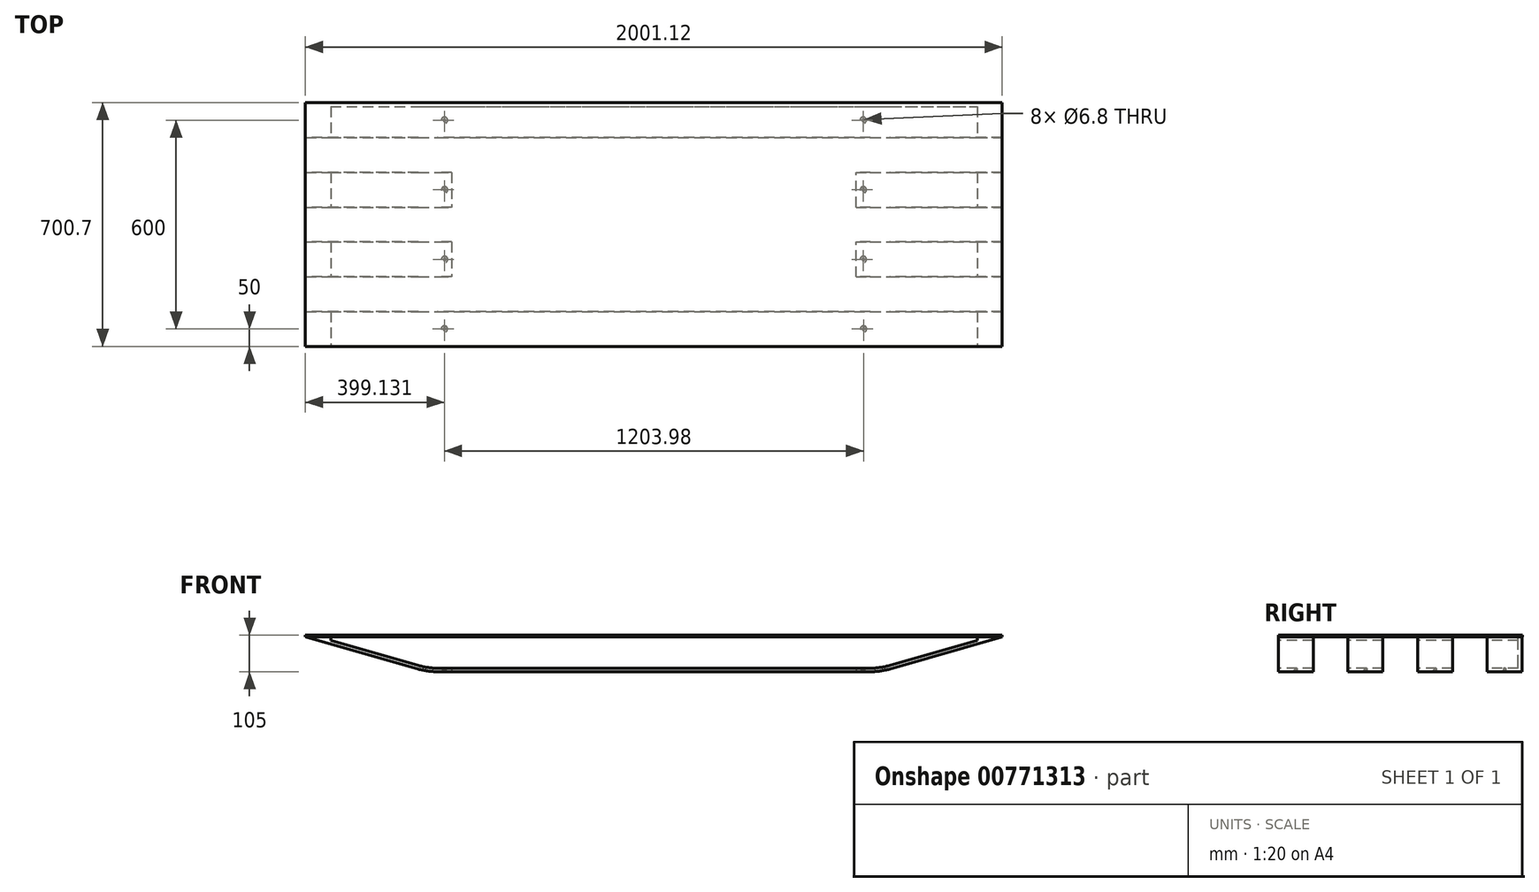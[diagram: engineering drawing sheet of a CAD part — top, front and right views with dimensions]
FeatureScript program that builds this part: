
annotation { "Feature Type Name" : "Feature", "Feature Type Description" : "" }
export const myFeature = defineFeature(function(context is Context, id is Id, definition is map)
    precondition{}
    {
        {
            var Q0;
            Q0=qCreatedBy(makeId("Front.planeOp"),FACE);
            var sketch = newSketch(context, id + "F0", { "sketchPlane" : qUnion([Q0])});
            skLineSegment(sketch, "E0.bottom", {"start": v(-1000, 50) * mm, "end": v(1000, 50) * mm});
            skLineSegment(sketch, "E0.top", {"start": v(-650, -50) * mm, "end": v(650, -50) * mm});
            skPoint(sketch, "E0.middle", {"position": v(0, 0) * mm});
            skLineSegment(sketch, "E1", {"start": v(-1000, 50) * mm, "end": v(-650, -50) * mm});
            skLineSegment(sketch, "E2", {"start": v(650, -50) * mm, "end": v(1000, 50) * mm});
            skPoint(sketch, "E0.left.end.orphan", {"position": v(-1000, -50) * mm});
            skPoint(sketch, "E0.right.end.orphan", {"position": v(1000, -50) * mm});
            skSolve(sketch);
        }
        {
            var Q0;
            Q0=makeQuery(id+"F0.imprint","IMPRINT",FACE,{"disambiguationData":[TD([[makeQuery(id+"F0.imprint","IMPRINT",EDGE,{"derivedFrom":sQuery(id+"F0.wireOp",EDGE,"E0.bottom")}),-1.0]])]});
            extrude(context, id + "F1", {"entities" : qUnion([Q0]), "oppositeDirection" : true, "depth" : 700 * mm, "offsetDistance" : 25 * mm});
        }
        {
            var Q0;
            Q0=makeQuery(id+"F1.opExtrude","SWEPT_FACE",FACE,{"disambiguationData":[OSD([sQuery(id+"F0.wireOp",EDGE,"E0.bottom")])]});
            var sketch = newSketch(context, id + "F2", { "sketchPlane" : qUnion([Q0])});
            skLineSegment(sketch, "E3", {"start": v(-1000, 600) * mm, "end": v(1000, 600) * mm});
            skLineSegment(sketch, "E4", {"start": v(-1000, 500) * mm, "end": v(1000, 500) * mm});
            skLineSegment(sketch, "E5", {"start": v(-1000, 400) * mm, "end": v(1000, 400) * mm});
            skLineSegment(sketch, "E6", {"start": v(-1000, 300) * mm, "end": v(1000, 300) * mm});
            skLineSegment(sketch, "E7", {"start": v(-1000, 200) * mm, "end": v(1000, 200) * mm});
            skLineSegment(sketch, "E8", {"start": v(-1000, 100) * mm, "end": v(1000, 100) * mm});
            skSolve(sketch);
        }
        {
            var Q0;
            {var subQ0=sQuery(id+"F2.wireOp",EDGE,"E3");Q0=makeQuery(id+"F2.imprint","IMPRINT",FACE,{"disambiguationData":[TD([[makeQuery(id+"F2.imprint","IMPRINT",EDGE,{"derivedFrom":subQ0}),-1.0]])]});}
            var Q1;
            {var subQ0=sQuery(id+"F2.wireOp",EDGE,"E5");Q1=makeQuery(id+"F2.imprint","IMPRINT",FACE,{"disambiguationData":[TD([[makeQuery(id+"F2.imprint","IMPRINT",EDGE,{"derivedFrom":subQ0}),-1.0]])]});}
            var Q2;
            {var subQ0=sQuery(id+"F2.wireOp",EDGE,"E7");Q2=makeQuery(id+"F2.imprint","IMPRINT",FACE,{"disambiguationData":[TD([[makeQuery(id+"F2.imprint","IMPRINT",EDGE,{"derivedFrom":subQ0}),-1.0]])]});}
            extrude(context, id + "F3", {"entities" : qUnion([Q0, Q1, Q2]), "operationType" : NewBodyOperationType.REMOVE, "oppositeDirection" : true, "depth" : 680 * mm, "offsetDistance" : 25 * mm});
        }
        {
            var Q0;
            Q0=makeQuery(id+"F1.opExtrude","CAP_FACE",FACE,{"disambiguationData":[OSD([sQuery(id+"F0.wireOp",EDGE,"E0.bottom"),sQuery(id+"F0.wireOp",EDGE,"E0.top"),sQuery(id+"F0.wireOp",EDGE,"E1"),sQuery(id+"F0.wireOp",EDGE,"E2")])],"isStart":true});
            var sketch = newSketch(context, id + "F4", { "sketchPlane" : qUnion([Q0])});
            skLineSegment(sketch, "E9.0", {"start": v(-928.6, 40) * mm, "end": v(928.6, 40) * mm});
            skLineSegment(sketch, "E9.1", {"start": v(-928.6, 40) * mm, "end": v(-648.6, -40) * mm});
            skLineSegment(sketch, "E9.2", {"start": v(-648.6, -40) * mm, "end": v(648.6, -40) * mm});
            skLineSegment(sketch, "E9.3", {"start": v(648.6, -40) * mm, "end": v(928.6, 40) * mm});
            skLineSegment(sketch, "E10", {"start": v(-928.6, 40) * mm, "end": v(-928.6, 50) * mm});
            skLineSegment(sketch, "E11", {"start": v(928.6, 40) * mm, "end": v(928.6, 50) * mm});
            skSolve(sketch);
        }
        {
            var Q0;
            Q0=makeQuery(id+"F4.imprint","IMPRINT",FACE,{"disambiguationData":[TD([[makeQuery(id+"F4.imprint","IMPRINT",EDGE,{"derivedFrom":sQuery(id+"F4.wireOp",EDGE,"E9.0")}),-1.0]])]});
            var Q1;
            Q1=makeQuery(id+"F4.imprint","IMPRINT",FACE,{"disambiguationData":[TD([[makeQuery(id+"F4.imprint","IMPRINT",EDGE,{"derivedFrom":sQuery(id+"F4.wireOp",EDGE,"E9.0")}),1.0]])]});
            extrude(context, id + "F5", {"entities" : qUnion([Q0, Q1]), "operationType" : NewBodyOperationType.REMOVE, "oppositeDirection" : true, "depth" : 689 * mm, "offsetDistance" : 25 * mm});
        }
        {
            var Q0;
            {var subQ2=sQuery(id+"F0.wireOp",EDGE,"E0.bottom");Q0=makeQuery(id+"F3.boolean.opBoolean","SPLIT",FACE,{"disambiguationData":[TD([makeQuery(id+"F3.opExtrude","SWEPT_FACE",FACE,{"disambiguationData":[OSD([sQuery(id+"F2.wireOp",EDGE,"E3")])]})])],"derivedFrom":makeQuery(id+"F1.opExtrude","SWEPT_FACE",FACE,{"disambiguationData":[OSD([subQ2])]})});}
            var sketch = newSketch(context, id + "F6", { "sketchPlane" : qUnion([Q0])});
            skLineSegment(sketch, "E12.bottom", {"start": v(-1000, 700) * mm, "end": v(1000.38, 700) * mm});
            skLineSegment(sketch, "E12.top", {"start": v(-1000, 0) * mm, "end": v(1000.38, 0) * mm});
            skLineSegment(sketch, "E12.left", {"start": v(-1000, 700) * mm, "end": v(-1000, 0) * mm});
            skLineSegment(sketch, "E12.right", {"start": v(1000.38, 700) * mm, "end": v(1000.38, 0) * mm});
            skLineSegment(sketch, "E13.0", {"start": v(-930, 680) * mm, "end": v(-930, 20) * mm});
            skLineSegment(sketch, "E13.1", {"start": v(-930, 680) * mm, "end": v(930.38, 680) * mm});
            skLineSegment(sketch, "E13.2", {"start": v(930.38, 680) * mm, "end": v(930.38, 20) * mm});
            skLineSegment(sketch, "E13.3", {"start": v(-930, 20) * mm, "end": v(930.38, 20) * mm});
            skSolve(sketch);
        }
        {
            var Q0;
            {var subQ0=sQuery(id+"F0.wireOp",EDGE,"E0.bottom");var subQ29=makeQuery(id+"F5.boolean.opBoolean","COPY",EDGE,{"derivedFrom":makeQuery(id+"F5.opExtrude","CAP_EDGE",EDGE,{"disambiguationData":[OSD([subQ0])],"isStart":false})});Q0=makeQuery(id+"F6.imprint","IMPRINT",FACE,{"disambiguationData":[TD([[makeQuery(id+"F6.imprint","IMPRINT",EDGE,{"derivedFrom":subQ29}),1.0]])]});}
            var Q1;
            {var subQ13=sQuery(id+"F6.wireOp",EDGE,"E12.top");Q1=makeQuery(id+"F6.imprint","IMPRINT",FACE,{"disambiguationData":[TD([[makeQuery(id+"F6.imprint","IMPRINT",EDGE,{"derivedFrom":subQ13}),1.0]])]});}
            extrude(context, id + "F7", {"entities" : qUnion([Q0, Q1]), "depth" : 10 * mm, "offsetDistance" : 25 * mm});
        }
        {
            var Q0;
            {var subQ0=sQuery(id+"F0.wireOp",EDGE,"E0.top");var subQ1=sQuery(id+"F0.wireOp",EDGE,"E1");Q0=makeQuery(id+"F3.boolean.opBoolean","SPLIT",EDGE,{"disambiguationData":[TD([makeQuery(id+"F3.opExtrude","SWEPT_FACE",FACE,{"disambiguationData":[OSD([sQuery(id+"F2.wireOp",EDGE,"E6")])]})])],"derivedFrom":makeQuery(id+"F1.opExtrude","SWEPT_EDGE",EDGE,{"disambiguationData":[OSD([subQ0,subQ1])]})});}
            var Q1;
            {var subQ0=sQuery(id+"F0.wireOp",EDGE,"E1");var subQ1=sQuery(id+"F0.wireOp",EDGE,"E0.top");Q1=makeQuery(id+"F3.boolean.opBoolean","SPLIT",EDGE,{"disambiguationData":[TD([makeQuery(id+"F3.opExtrude","SWEPT_FACE",FACE,{"disambiguationData":[OSD([sQuery(id+"F2.wireOp",EDGE,"E8")])]})])],"derivedFrom":makeQuery(id+"F1.opExtrude","SWEPT_EDGE",EDGE,{"disambiguationData":[OSD([subQ1,subQ0])]})});}
            var Q2;
            {var subQ0=sQuery(id+"F0.wireOp",EDGE,"E0.top");var subQ1=sQuery(id+"F0.wireOp",EDGE,"E1");Q2=makeQuery(id+"F3.boolean.opBoolean","SPLIT",EDGE,{"disambiguationData":[TD([makeQuery(id+"F3.opExtrude","SWEPT_FACE",FACE,{"disambiguationData":[OSD([sQuery(id+"F2.wireOp",EDGE,"E4")])]})])],"derivedFrom":makeQuery(id+"F1.opExtrude","SWEPT_EDGE",EDGE,{"disambiguationData":[OSD([subQ0,subQ1])]})});}
            var Q3;
            {var subQ0=sQuery(id+"F0.wireOp",EDGE,"E1");var subQ1=sQuery(id+"F0.wireOp",EDGE,"E0.top");Q3=makeQuery(id+"F3.boolean.opBoolean","SPLIT",EDGE,{"disambiguationData":[TD([makeQuery(id+"F3.opExtrude","SWEPT_FACE",FACE,{"disambiguationData":[OSD([sQuery(id+"F2.wireOp",EDGE,"E3")])]})])],"derivedFrom":makeQuery(id+"F1.opExtrude","SWEPT_EDGE",EDGE,{"disambiguationData":[OSD([subQ1,subQ0])]})});}
            var Q4;
            {var subQ0=sQuery(id+"F0.wireOp",EDGE,"E2");var subQ1=sQuery(id+"F0.wireOp",EDGE,"E0.top");Q4=makeQuery(id+"F3.boolean.opBoolean","SPLIT",EDGE,{"disambiguationData":[TD([makeQuery(id+"F3.opExtrude","SWEPT_FACE",FACE,{"disambiguationData":[OSD([sQuery(id+"F2.wireOp",EDGE,"E3")])]})])],"derivedFrom":makeQuery(id+"F1.opExtrude","SWEPT_EDGE",EDGE,{"disambiguationData":[OSD([subQ1,subQ0])]})});}
            var Q5;
            {var subQ0=sQuery(id+"F0.wireOp",EDGE,"E0.top");var subQ1=sQuery(id+"F0.wireOp",EDGE,"E2");Q5=makeQuery(id+"F3.boolean.opBoolean","SPLIT",EDGE,{"disambiguationData":[TD([makeQuery(id+"F3.opExtrude","SWEPT_FACE",FACE,{"disambiguationData":[OSD([sQuery(id+"F2.wireOp",EDGE,"E4")])]})])],"derivedFrom":makeQuery(id+"F1.opExtrude","SWEPT_EDGE",EDGE,{"disambiguationData":[OSD([subQ0,subQ1])]})});}
            var Q6;
            {var subQ0=sQuery(id+"F0.wireOp",EDGE,"E0.top");var subQ1=sQuery(id+"F0.wireOp",EDGE,"E2");Q6=makeQuery(id+"F3.boolean.opBoolean","SPLIT",EDGE,{"disambiguationData":[TD([makeQuery(id+"F3.opExtrude","SWEPT_FACE",FACE,{"disambiguationData":[OSD([sQuery(id+"F2.wireOp",EDGE,"E6")])]})])],"derivedFrom":makeQuery(id+"F1.opExtrude","SWEPT_EDGE",EDGE,{"disambiguationData":[OSD([subQ0,subQ1])]})});}
            var Q7;
            {var subQ0=sQuery(id+"F0.wireOp",EDGE,"E2");var subQ1=sQuery(id+"F0.wireOp",EDGE,"E0.top");Q7=makeQuery(id+"F3.boolean.opBoolean","SPLIT",EDGE,{"disambiguationData":[TD([makeQuery(id+"F3.opExtrude","SWEPT_FACE",FACE,{"disambiguationData":[OSD([sQuery(id+"F2.wireOp",EDGE,"E8")])]})])],"derivedFrom":makeQuery(id+"F1.opExtrude","SWEPT_EDGE",EDGE,{"disambiguationData":[OSD([subQ1,subQ0])]})});}
            var Q8;
            {var subQ0=sQuery(id+"F4.wireOp",EDGE,"E9.1");var subQ1=sQuery(id+"F4.wireOp",EDGE,"E9.2");Q8=makeQuery(id+"F5.boolean.opBoolean","COPY",EDGE,{"disambiguationData":[TD([makeQuery(id+"F3.boolean.opBoolean","COPY",FACE,{"derivedFrom":makeQuery(id+"F3.opExtrude","SWEPT_FACE",FACE,{"disambiguationData":[OSD([sQuery(id+"F2.wireOp",EDGE,"E6")])]})})])],"derivedFrom":makeQuery(id+"F5.opExtrude","SWEPT_EDGE",EDGE,{"disambiguationData":[OSD([subQ0,subQ1])]})});}
            var Q9;
            {var subQ0=sQuery(id+"F4.wireOp",EDGE,"E9.1");var subQ1=sQuery(id+"F4.wireOp",EDGE,"E9.2");Q9=makeQuery(id+"F5.boolean.opBoolean","COPY",EDGE,{"disambiguationData":[TD([makeQuery(id+"F3.boolean.opBoolean","COPY",FACE,{"derivedFrom":makeQuery(id+"F3.opExtrude","SWEPT_FACE",FACE,{"disambiguationData":[OSD([sQuery(id+"F2.wireOp",EDGE,"E8")])]})})])],"derivedFrom":makeQuery(id+"F5.opExtrude","SWEPT_EDGE",EDGE,{"disambiguationData":[OSD([subQ0,subQ1])]})});}
            var Q10;
            {var subQ0=sQuery(id+"F4.wireOp",EDGE,"E9.2");var subQ1=sQuery(id+"F4.wireOp",EDGE,"E9.1");Q10=makeQuery(id+"F5.boolean.opBoolean","COPY",EDGE,{"disambiguationData":[TD([makeQuery(id+"F3.boolean.opBoolean","COPY",FACE,{"derivedFrom":makeQuery(id+"F3.opExtrude","SWEPT_FACE",FACE,{"disambiguationData":[OSD([sQuery(id+"F2.wireOp",EDGE,"E4")])]})})])],"derivedFrom":makeQuery(id+"F5.opExtrude","SWEPT_EDGE",EDGE,{"disambiguationData":[OSD([subQ1,subQ0])]})});}
            var Q11;
            {var subQ0=sQuery(id+"F4.wireOp",EDGE,"E9.2");var subQ1=sQuery(id+"F4.wireOp",EDGE,"E9.1");Q11=makeQuery(id+"F5.boolean.opBoolean","COPY",EDGE,{"disambiguationData":[TD([makeQuery(id+"F3.boolean.opBoolean","COPY",FACE,{"derivedFrom":makeQuery(id+"F3.opExtrude","SWEPT_FACE",FACE,{"disambiguationData":[OSD([sQuery(id+"F2.wireOp",EDGE,"E3")])]})})])],"derivedFrom":makeQuery(id+"F5.opExtrude","SWEPT_EDGE",EDGE,{"disambiguationData":[OSD([subQ1,subQ0])]})});}
            var Q12;
            {var subQ0=sQuery(id+"F4.wireOp",EDGE,"E9.2");var subQ1=sQuery(id+"F4.wireOp",EDGE,"E9.3");Q12=makeQuery(id+"F5.boolean.opBoolean","COPY",EDGE,{"disambiguationData":[TD([makeQuery(id+"F3.boolean.opBoolean","COPY",FACE,{"derivedFrom":makeQuery(id+"F3.opExtrude","SWEPT_FACE",FACE,{"disambiguationData":[OSD([sQuery(id+"F2.wireOp",EDGE,"E6")])]})})])],"derivedFrom":makeQuery(id+"F5.opExtrude","SWEPT_EDGE",EDGE,{"disambiguationData":[OSD([subQ0,subQ1])]})});}
            var Q13;
            {var subQ0=sQuery(id+"F4.wireOp",EDGE,"E9.3");var subQ1=sQuery(id+"F4.wireOp",EDGE,"E9.2");Q13=makeQuery(id+"F5.boolean.opBoolean","COPY",EDGE,{"disambiguationData":[TD([makeQuery(id+"F3.boolean.opBoolean","COPY",FACE,{"derivedFrom":makeQuery(id+"F3.opExtrude","SWEPT_FACE",FACE,{"disambiguationData":[OSD([sQuery(id+"F2.wireOp",EDGE,"E8")])]})})])],"derivedFrom":makeQuery(id+"F5.opExtrude","SWEPT_EDGE",EDGE,{"disambiguationData":[OSD([subQ1,subQ0])]})});}
            var Q14;
            {var subQ0=sQuery(id+"F4.wireOp",EDGE,"E9.3");var subQ1=sQuery(id+"F4.wireOp",EDGE,"E9.2");Q14=makeQuery(id+"F5.boolean.opBoolean","COPY",EDGE,{"disambiguationData":[TD([makeQuery(id+"F3.boolean.opBoolean","COPY",FACE,{"derivedFrom":makeQuery(id+"F3.opExtrude","SWEPT_FACE",FACE,{"disambiguationData":[OSD([sQuery(id+"F2.wireOp",EDGE,"E3")])]})})])],"derivedFrom":makeQuery(id+"F5.opExtrude","SWEPT_EDGE",EDGE,{"disambiguationData":[OSD([subQ1,subQ0])]})});}
            fillet(context, id + "F8", {"entities" : qUnion([Q0, Q1, Q2, Q3, Q4, Q5, Q6, Q7, Q8, Q9, Q10, Q11, Q12, Q13, Q14]), "radius" : 200 * mm, "tangentPropagation" : true, "allowEdgeOverflow" : false});
        }
        {
            var Q0;
            {var subQ0=sQuery(id+"F4.wireOp",EDGE,"E9.2");var subQ1=sQuery(id+"F4.wireOp",EDGE,"E9.3");Q0=makeQuery(id+"F5.boolean.opBoolean","COPY",EDGE,{"disambiguationData":[TD([makeQuery(id+"F3.boolean.opBoolean","COPY",FACE,{"derivedFrom":makeQuery(id+"F3.opExtrude","SWEPT_FACE",FACE,{"disambiguationData":[OSD([sQuery(id+"F2.wireOp",EDGE,"E4")])]})})])],"derivedFrom":makeQuery(id+"F5.opExtrude","SWEPT_EDGE",EDGE,{"disambiguationData":[OSD([subQ0,subQ1])]})});}
            fillet(context, id + "F9", {"entities" : qUnion([Q0]), "radius" : 200 * mm, "tangentPropagation" : true, "allowEdgeOverflow" : false});
        }
        {
            var Q0;
            Q0=makeQuery(id+"F7.opExtrude","SWEPT_BODY",BODY,{"disambiguationData":[OSD([sQuery(id+"F0.wireOp",EDGE,"E0.bottom"),sQuery(id+"F4.wireOp",EDGE,"E10"),sQuery(id+"F4.wireOp",EDGE,"E11"),sQuery(id+"F6.wireOp",EDGE,"E12.bottom"),sQuery(id+"F6.wireOp",EDGE,"E12.top"),sQuery(id+"F6.wireOp",EDGE,"E12.left"),sQuery(id+"F6.wireOp",EDGE,"E12.right"),sQuery(id+"F6.wireOp",EDGE,"E13.0"),sQuery(id+"F6.wireOp",EDGE,"E13.1"),sQuery(id+"F6.wireOp",EDGE,"E13.2"),sQuery(id+"F6.wireOp",EDGE,"E13.3")])]});
            deleteBodies(context, id + "F10", {"entities" : qUnion([Q0])});
        }
        {
            var Q0;
            Q0=makeQuery(id+"F5.boolean.opBoolean","COPY",FACE,{"disambiguationData":[TD([makeQuery(id+"F3.boolean.opBoolean","COPY",FACE,{"derivedFrom":makeQuery(id+"F3.opExtrude","SWEPT_FACE",FACE,{"disambiguationData":[OSD([sQuery(id+"F2.wireOp",EDGE,"E6")])]})})])],"derivedFrom":makeQuery(id+"F5.opExtrude","SWEPT_FACE",FACE,{"disambiguationData":[OSD([sQuery(id+"F4.wireOp",EDGE,"E9.2")])]})});
            var sketch = newSketch(context, id + "F11", { "sketchPlane" : qUnion([Q0])});
            skLineSegment(sketch, "E14.bottom", {"start": v(-580.59, 506.37) * mm, "end": v(580.59, 506.37) * mm});
            skLineSegment(sketch, "E14.top", {"start": v(-580.59, 152.95) * mm, "end": v(580.59, 152.95) * mm});
            skLineSegment(sketch, "E14.left", {"start": v(-580.59, 506.37) * mm, "end": v(-580.59, 152.95) * mm});
            skLineSegment(sketch, "E14.right", {"start": v(580.59, 506.37) * mm, "end": v(580.59, 152.95) * mm});
            skSolve(sketch);
        }
        {
            var Q0;
            {var subQ0=sQuery(id+"F11.wireOp",EDGE,"E14.bottom");Q0=makeQuery(id+"F11.imprint","IMPRINT",FACE,{"disambiguationData":[TD([[makeQuery(id+"F11.imprint","IMPRINT",EDGE,{"derivedFrom":subQ0}),-1.0]])]});}
            var Q1;
            {var subQ0=sQuery(id+"F11.wireOp",EDGE,"E14.left");var subQ1=makeQuery(id+"F5.opExtrude","SWEPT_FACE",FACE,{"disambiguationData":[OSD([sQuery(id+"F4.wireOp",EDGE,"E9.2")])]});var subQ2=makeQuery(id+"F5.boolean.opBoolean","INTERSECT",EDGE,{"derivedFrom":[makeQuery(id+"F3.boolean.opBoolean","COPY",FACE,{"derivedFrom":makeQuery(id+"F3.opExtrude","SWEPT_FACE",FACE,{"disambiguationData":[OSD([sQuery(id+"F2.wireOp",EDGE,"E6")])]})}),subQ1]});var subQ3=makeQuery(id+"F11.imprint","INTERSECT",VERTEX,{"derivedFrom":[subQ2,subQ0]});Q1=makeQuery(id+"F11.imprint","IMPRINT",FACE,{"disambiguationData":[TD([[makeQuery(id+"F11.imprint","IMPRINT",EDGE,{"disambiguationData":[TD([[subQ3,-1.0]])],"derivedFrom":subQ0}),1.0]])]});}
            var Q2;
            {var subQ0=sQuery(id+"F11.wireOp",EDGE,"E14.top");Q2=makeQuery(id+"F11.imprint","IMPRINT",FACE,{"disambiguationData":[TD([[makeQuery(id+"F11.imprint","IMPRINT",EDGE,{"derivedFrom":subQ0}),1.0]])]});}
            extrude(context, id + "F12", {"entities" : qUnion([Q0, Q1, Q2]), "operationType" : NewBodyOperationType.REMOVE, "oppositeDirection" : true, "depth" : 175 * mm, "offsetDistance" : 25 * mm});
        }
        {
            var Q0;
            {var subQ0=makeQuery(id+"F3.opExtrude","SWEPT_FACE",FACE,{"disambiguationData":[OSD([sQuery(id+"F2.wireOp",EDGE,"E6")])]});var subQ1=sQuery(id+"F0.wireOp",EDGE,"E0.top");var subQ2=makeQuery(id+"F1.opExtrude","SWEPT_FACE",FACE,{"disambiguationData":[OSD([subQ1])]});Q0=makeQuery(id+"F12.boolean.opBoolean","SPLIT",FACE,{"disambiguationData":[TD([makeQuery(id+"F12.opExtrude","SWEPT_FACE",FACE,{"disambiguationData":[OSD([sQuery(id+"F11.wireOp",EDGE,"E14.left")])]})])],"derivedFrom":makeQuery(id+"F3.boolean.opBoolean","SPLIT",FACE,{"disambiguationData":[TD([subQ0])],"derivedFrom":subQ2})});}
            var sketch = newSketch(context, id + "F13", { "sketchPlane" : qUnion([Q0])});
            skPoint(sketch, "E15", {"position": v(-601.29, -250) * mm});
            skPoint(sketch, "E15.positionSnap0", {"position": v(-601.29, -300) * mm});
            skPoint(sketch, "E15.positionSnap1", {"position": v(-580.59, -250) * mm});
            skSolve(sketch);
        }
        {
            var Q0;
            Q0=sQuery(id+"F13.wireOp",VERTEX,"E15");
            var Q1;
            Q1=makeQuery(id+"F12.boolean.opBoolean","SPLIT",BODY,{"disambiguationData":[OD(0.0)],"derivedFrom":makeQuery(id+"F3.boolean.opBoolean","SPLIT",BODY,{"disambiguationData":[OD(3.0)],"derivedFrom":makeQuery(id+"F1.opExtrude","SWEPT_BODY",BODY,{"disambiguationData":[OSD([sQuery(id+"F0.wireOp",EDGE,"E0.bottom"),sQuery(id+"F0.wireOp",EDGE,"E0.top"),sQuery(id+"F0.wireOp",EDGE,"E1"),sQuery(id+"F0.wireOp",EDGE,"E2")])]})})});
            hole(context, id + "F14", {"style" : HoleStyle.C_SINK, "endStyle" : HoleEndStyle.BLIND, "standardTappedOrClearance" : lookupTablePath({ "standard" : "ISO", "engagement" : "75%", "pitch" : "1.25 mm", "size" : "M8", "type" : "Tapped" }), "standardBlindInLast" : lookupTablePath({ "standard" : "ISO", "engagement" : "75%", "pitch" : "1.25 mm", "size" : "M8", "type" : "Tapped" }), "holeDiameter" : 6.8 * mm, "cSinkDiameter" : 17.92 * mm, "cSinkAngle" : 90 * degree, "majorDiameter" : 8 * mm, "showTappedDepth" : true, "holeDepth" : 15.75 * mm, "isTappedThrough" : true, "tappedDepth" : 12 * mm, "tapClearance" : 3, "locations" : qUnion([Q0]), "scope" : qUnion([Q1])});
        }
        {
            var Q0;
            {var subQ0=makeQuery(id+"F3.opExtrude","SWEPT_FACE",FACE,{"disambiguationData":[OSD([sQuery(id+"F2.wireOp",EDGE,"E4")])]});var subQ2=sQuery(id+"F0.wireOp",EDGE,"E0.top");var subQ3=makeQuery(id+"F1.opExtrude","SWEPT_FACE",FACE,{"disambiguationData":[OSD([subQ2])]});Q0=makeQuery(id+"F12.boolean.opBoolean","SPLIT",FACE,{"disambiguationData":[TD([makeQuery(id+"F12.opExtrude","SWEPT_FACE",FACE,{"disambiguationData":[OSD([sQuery(id+"F11.wireOp",EDGE,"E14.left")])]})])],"derivedFrom":makeQuery(id+"F3.boolean.opBoolean","SPLIT",FACE,{"disambiguationData":[TD([subQ0])],"derivedFrom":subQ3})});}
            var sketch = newSketch(context, id + "F15", { "sketchPlane" : qUnion([Q0])});
            skPoint(sketch, "E16", {"position": v(-601.29, -450) * mm});
            skPoint(sketch, "E16.positionSnap0", {"position": v(-601.29, -400) * mm});
            skPoint(sketch, "E16.positionSnap1", {"position": v(-580.59, -450) * mm});
            skSolve(sketch);
        }
        {
            var Q0;
            Q0=sQuery(id+"F15.wireOp",VERTEX,"E16");
            var Q1;
            Q1=makeQuery(id+"F12.boolean.opBoolean","SPLIT",BODY,{"disambiguationData":[OD(0.0)],"derivedFrom":makeQuery(id+"F3.boolean.opBoolean","SPLIT",BODY,{"disambiguationData":[OD(2.0)],"derivedFrom":makeQuery(id+"F1.opExtrude","SWEPT_BODY",BODY,{"disambiguationData":[OSD([sQuery(id+"F0.wireOp",EDGE,"E0.bottom"),sQuery(id+"F0.wireOp",EDGE,"E0.top"),sQuery(id+"F0.wireOp",EDGE,"E1"),sQuery(id+"F0.wireOp",EDGE,"E2")])]})})});
            hole(context, id + "F16", {"style" : HoleStyle.C_SINK, "endStyle" : HoleEndStyle.BLIND, "standardTappedOrClearance" : lookupTablePath({ "standard" : "ISO", "engagement" : "75%", "pitch" : "1.25 mm", "size" : "M8", "type" : "Tapped" }), "standardBlindInLast" : lookupTablePath({ "standard" : "ISO", "engagement" : "75%", "pitch" : "1.25 mm", "size" : "M8", "type" : "Tapped" }), "holeDiameter" : 6.8 * mm, "cSinkDiameter" : 17.92 * mm, "cSinkAngle" : 90 * degree, "majorDiameter" : 8 * mm, "showTappedDepth" : true, "holeDepth" : 15.75 * mm, "isTappedThrough" : true, "tappedDepth" : 12 * mm, "tapClearance" : 3, "locations" : qUnion([Q0]), "scope" : qUnion([Q1])});
        }
        {
            var Q0;
            {var subQ2=sQuery(id+"F0.wireOp",EDGE,"E0.top");Q0=makeQuery(id+"F3.boolean.opBoolean","SPLIT",FACE,{"disambiguationData":[TD([makeQuery(id+"F3.opExtrude","SWEPT_FACE",FACE,{"disambiguationData":[OSD([sQuery(id+"F2.wireOp",EDGE,"E3")])]})])],"derivedFrom":makeQuery(id+"F1.opExtrude","SWEPT_FACE",FACE,{"disambiguationData":[OSD([subQ2])]})});}
            var sketch = newSketch(context, id + "F17", { "sketchPlane" : qUnion([Q0])});
            skLineSegment(sketch, "E17", {"start": v(-578.49, -496.36) * mm, "end": v(-578.49, -700) * mm, "construction": true});
            skPoint(sketch, "E18", {"position": v(-601.77, -650) * mm});
            skPoint(sketch, "E18.positionSnap0", {"position": v(-621.99, -650) * mm});
            skLineSegment(sketch, "E19", {"start": v(-601.77, -650) * mm, "end": v(600.86, -650) * mm});
            skSolve(sketch);
        }
        {
            var Q0;
            Q0=sQuery(id+"F17.wireOp",VERTEX,"E18");
            var Q1;
            Q1=sQuery(id+"F17.wireOp",VERTEX,"E19.end");
            var Q2;
            Q2=makeQuery(id+"F3.boolean.opBoolean","SPLIT",BODY,{"disambiguationData":[OD(1.0)],"derivedFrom":makeQuery(id+"F1.opExtrude","SWEPT_BODY",BODY,{"disambiguationData":[OSD([sQuery(id+"F0.wireOp",EDGE,"E0.bottom"),sQuery(id+"F0.wireOp",EDGE,"E0.top"),sQuery(id+"F0.wireOp",EDGE,"E1"),sQuery(id+"F0.wireOp",EDGE,"E2")])]})});
            hole(context, id + "F18", {"style" : HoleStyle.C_SINK, "endStyle" : HoleEndStyle.BLIND, "standardTappedOrClearance" : lookupTablePath({ "standard" : "ISO", "engagement" : "75%", "pitch" : "1.25 mm", "size" : "M8", "type" : "Tapped" }), "standardBlindInLast" : lookupTablePath({ "standard" : "ISO", "engagement" : "75%", "pitch" : "1.25 mm", "size" : "M8", "type" : "Tapped" }), "holeDiameter" : 6.8 * mm, "cSinkDiameter" : 17.92 * mm, "cSinkAngle" : 90 * degree, "majorDiameter" : 8 * mm, "showTappedDepth" : true, "holeDepth" : 15.75 * mm, "isTappedThrough" : true, "tappedDepth" : 12 * mm, "tapClearance" : 3, "locations" : qUnion([Q0, Q1]), "scope" : qUnion([Q2])});
        }
        {
            var Q0;
            {var subQ0=sQuery(id+"F0.wireOp",EDGE,"E2");var subQ2=sQuery(id+"F0.wireOp",EDGE,"E0.bottom");var subQ4=makeQuery(id+"F1.opExtrude","SWEPT_FACE",FACE,{"disambiguationData":[OSD([subQ0])]});var subQ5=makeQuery(id+"F3.opExtrude","SWEPT_FACE",FACE,{"disambiguationData":[OSD([sQuery(id+"F2.wireOp",EDGE,"E8")])]});Q0=makeQuery(id+"F5.boolean.opBoolean","SPLIT",FACE,{"disambiguationData":[TD([subQ4])],"derivedFrom":makeQuery(id+"F3.boolean.opBoolean","SPLIT",FACE,{"disambiguationData":[TD([subQ5])],"derivedFrom":makeQuery(id+"F1.opExtrude","SWEPT_FACE",FACE,{"disambiguationData":[OSD([subQ2])]})})});}
            var sketch = newSketch(context, id + "F19", { "sketchPlane" : qUnion([Q0])});
            skLineSegment(sketch, "E20.bottom", {"start": v(1000, 0) * mm, "end": v(-1001.12, 0) * mm});
            skLineSegment(sketch, "E20.top", {"start": v(1000, 700.7) * mm, "end": v(-1001.12, 700.7) * mm});
            skLineSegment(sketch, "E20.left", {"start": v(1000, 0) * mm, "end": v(1000, 700.7) * mm});
            skLineSegment(sketch, "E20.right", {"start": v(-1001.12, 0) * mm, "end": v(-1001.12, 700.7) * mm});
            skSolve(sketch);
        }
        {
            var Q0;
            {var subQ5=sQuery(id+"F0.wireOp",EDGE,"E2");var subQ6=sQuery(id+"F2.wireOp",EDGE,"E8");var subQ11=makeQuery(id+"F5.boolean.opBoolean","SPLIT",EDGE,{"disambiguationData":[TD([makeQuery(id+"F1.opExtrude","SWEPT_FACE",FACE,{"disambiguationData":[OSD([subQ5])]})])],"derivedFrom":makeQuery(id+"F3.boolean.opBoolean","COPY",EDGE,{"derivedFrom":makeQuery(id+"F3.opExtrude","CAP_EDGE",EDGE,{"disambiguationData":[OSD([subQ6])],"isStart":true})})});Q0=makeQuery(id+"F19.imprint","IMPRINT",FACE,{"disambiguationData":[TD([[makeQuery(id+"F19.imprint","IMPRINT",EDGE,{"derivedFrom":subQ11}),-1.0]])]});}
            var Q1;
            {var subQ9=sQuery(id+"F19.wireOp",EDGE,"E20.top");Q1=makeQuery(id+"F19.imprint","IMPRINT",FACE,{"disambiguationData":[TD([[makeQuery(id+"F19.imprint","IMPRINT",EDGE,{"derivedFrom":subQ9}),1.0]])]});}
            extrude(context, id + "F20", {"entities" : qUnion([Q0, Q1]), "depth" : 5 * mm, "offsetDistance" : 25 * mm});
        }
        {
            var Q0;
            {var subQ0=makeQuery(id+"F3.opExtrude","SWEPT_FACE",FACE,{"disambiguationData":[OSD([sQuery(id+"F2.wireOp",EDGE,"E4")])]});var subQ2=sQuery(id+"F0.wireOp",EDGE,"E0.top");var subQ3=makeQuery(id+"F1.opExtrude","SWEPT_FACE",FACE,{"disambiguationData":[OSD([subQ2])]});Q0=makeQuery(id+"F12.boolean.opBoolean","SPLIT",FACE,{"disambiguationData":[TD([makeQuery(id+"F12.opExtrude","SWEPT_FACE",FACE,{"disambiguationData":[OSD([sQuery(id+"F11.wireOp",EDGE,"E14.right")])]})])],"derivedFrom":makeQuery(id+"F3.boolean.opBoolean","SPLIT",FACE,{"disambiguationData":[TD([subQ0])],"derivedFrom":subQ3})});}
            var sketch = newSketch(context, id + "F21", { "sketchPlane" : qUnion([Q0])});
            skPoint(sketch, "E21", {"position": v(601.29, -450) * mm});
            skPoint(sketch, "E21.positionSnap0", {"position": v(621.99, -450) * mm});
            skPoint(sketch, "E21.positionSnap1", {"position": v(601.29, -500) * mm});
            skSolve(sketch);
        }
        {
            var Q0;
            Q0=sQuery(id+"F21.wireOp",VERTEX,"E21");
            var Q1;
            Q1=makeQuery(id+"F12.boolean.opBoolean","SPLIT",BODY,{"disambiguationData":[OD(1.0)],"derivedFrom":makeQuery(id+"F3.boolean.opBoolean","SPLIT",BODY,{"disambiguationData":[OD(2.0)],"derivedFrom":makeQuery(id+"F1.opExtrude","SWEPT_BODY",BODY,{"disambiguationData":[OSD([sQuery(id+"F0.wireOp",EDGE,"E0.bottom"),sQuery(id+"F0.wireOp",EDGE,"E0.top"),sQuery(id+"F0.wireOp",EDGE,"E1"),sQuery(id+"F0.wireOp",EDGE,"E2")])]})})});
            hole(context, id + "F22", {"style" : HoleStyle.C_SINK, "endStyle" : HoleEndStyle.BLIND, "standardTappedOrClearance" : lookupTablePath({ "standard" : "ISO", "engagement" : "75%", "pitch" : "1.25 mm", "size" : "M8", "type" : "Tapped" }), "standardBlindInLast" : lookupTablePath({ "standard" : "ISO", "engagement" : "75%", "pitch" : "1.25 mm", "size" : "M8", "type" : "Tapped" }), "holeDiameter" : 6.8 * mm, "cSinkDiameter" : 17.92 * mm, "cSinkAngle" : 90 * degree, "majorDiameter" : 8 * mm, "showTappedDepth" : true, "holeDepth" : 15.75 * mm, "isTappedThrough" : true, "tappedDepth" : 12 * mm, "tapClearance" : 3, "locations" : qUnion([Q0]), "scope" : qUnion([Q1])});
        }
        {
            var Q0;
            {var subQ0=makeQuery(id+"F3.opExtrude","SWEPT_FACE",FACE,{"disambiguationData":[OSD([sQuery(id+"F2.wireOp",EDGE,"E6")])]});var subQ2=sQuery(id+"F0.wireOp",EDGE,"E0.top");var subQ3=makeQuery(id+"F1.opExtrude","SWEPT_FACE",FACE,{"disambiguationData":[OSD([subQ2])]});Q0=makeQuery(id+"F12.boolean.opBoolean","SPLIT",FACE,{"disambiguationData":[TD([makeQuery(id+"F12.opExtrude","SWEPT_FACE",FACE,{"disambiguationData":[OSD([sQuery(id+"F11.wireOp",EDGE,"E14.right")])]})])],"derivedFrom":makeQuery(id+"F3.boolean.opBoolean","SPLIT",FACE,{"disambiguationData":[TD([subQ0])],"derivedFrom":subQ3})});}
            var sketch = newSketch(context, id + "F23", { "sketchPlane" : qUnion([Q0])});
            skPoint(sketch, "E22", {"position": v(601.29, -250) * mm});
            skPoint(sketch, "E22.positionSnap0", {"position": v(601.29, -200) * mm});
            skPoint(sketch, "E22.positionSnap1", {"position": v(621.99, -250) * mm});
            skSolve(sketch);
        }
        {
            var Q0;
            Q0=sQuery(id+"F23.wireOp",VERTEX,"E22");
            var Q1;
            Q1=makeQuery(id+"F12.boolean.opBoolean","SPLIT",BODY,{"disambiguationData":[OD(1.0)],"derivedFrom":makeQuery(id+"F3.boolean.opBoolean","SPLIT",BODY,{"disambiguationData":[OD(3.0)],"derivedFrom":makeQuery(id+"F1.opExtrude","SWEPT_BODY",BODY,{"disambiguationData":[OSD([sQuery(id+"F0.wireOp",EDGE,"E0.bottom"),sQuery(id+"F0.wireOp",EDGE,"E0.top"),sQuery(id+"F0.wireOp",EDGE,"E1"),sQuery(id+"F0.wireOp",EDGE,"E2")])]})})});
            hole(context, id + "F24", {"style" : HoleStyle.C_SINK, "endStyle" : HoleEndStyle.BLIND, "standardTappedOrClearance" : lookupTablePath({ "standard" : "ISO", "engagement" : "75%", "pitch" : "1.25 mm", "size" : "M8", "type" : "Tapped" }), "standardBlindInLast" : lookupTablePath({ "standard" : "ISO", "engagement" : "75%", "pitch" : "1.25 mm", "size" : "M8", "type" : "Tapped" }), "holeDiameter" : 6.8 * mm, "cSinkDiameter" : 17.92 * mm, "cSinkAngle" : 90 * degree, "majorDiameter" : 8 * mm, "showTappedDepth" : true, "holeDepth" : 15.75 * mm, "isTappedThrough" : true, "tappedDepth" : 12 * mm, "tapClearance" : 3, "locations" : qUnion([Q0]), "scope" : qUnion([Q1])});
        }
        {
            var Q0;
            {var subQ2=sQuery(id+"F0.wireOp",EDGE,"E0.top");Q0=makeQuery(id+"F3.boolean.opBoolean","SPLIT",FACE,{"disambiguationData":[TD([makeQuery(id+"F3.opExtrude","SWEPT_FACE",FACE,{"disambiguationData":[OSD([sQuery(id+"F2.wireOp",EDGE,"E8")])]})])],"derivedFrom":makeQuery(id+"F1.opExtrude","SWEPT_FACE",FACE,{"disambiguationData":[OSD([subQ2])]})});}
            var sketch = newSketch(context, id + "F25", { "sketchPlane" : qUnion([Q0])});
            skLineSegment(sketch, "E23", {"start": v(-601.99, -50) * mm, "end": v(601.99, -50) * mm});
            skPoint(sketch, "E23.startSnap0", {"position": v(-621.99, -50) * mm});
            skSolve(sketch);
        }
        {
            var Q0;
            Q0=sQuery(id+"F25.wireOp",VERTEX,"E23.end");
            var Q1;
            Q1=sQuery(id+"F25.wireOp",VERTEX,"E23.start");
            var Q2;
            Q2=makeQuery(id+"F3.boolean.opBoolean","SPLIT",BODY,{"disambiguationData":[OD(0.0)],"derivedFrom":makeQuery(id+"F1.opExtrude","SWEPT_BODY",BODY,{"disambiguationData":[OSD([sQuery(id+"F0.wireOp",EDGE,"E0.bottom"),sQuery(id+"F0.wireOp",EDGE,"E0.top"),sQuery(id+"F0.wireOp",EDGE,"E1"),sQuery(id+"F0.wireOp",EDGE,"E2")])]})});
            hole(context, id + "F26", {"style" : HoleStyle.C_SINK, "endStyle" : HoleEndStyle.BLIND, "standardTappedOrClearance" : lookupTablePath({ "standard" : "ISO", "engagement" : "75%", "pitch" : "1.25 mm", "size" : "M8", "type" : "Tapped" }), "standardBlindInLast" : lookupTablePath({ "standard" : "ISO", "engagement" : "75%", "pitch" : "1.25 mm", "size" : "M8", "type" : "Tapped" }), "holeDiameter" : 6.8 * mm, "cSinkDiameter" : 17.92 * mm, "cSinkAngle" : 90 * degree, "majorDiameter" : 8 * mm, "showTappedDepth" : true, "holeDepth" : 15.75 * mm, "isTappedThrough" : true, "tappedDepth" : 12 * mm, "tapClearance" : 3, "locations" : qUnion([Q0, Q1]), "scope" : qUnion([Q2])});
        }
    });
